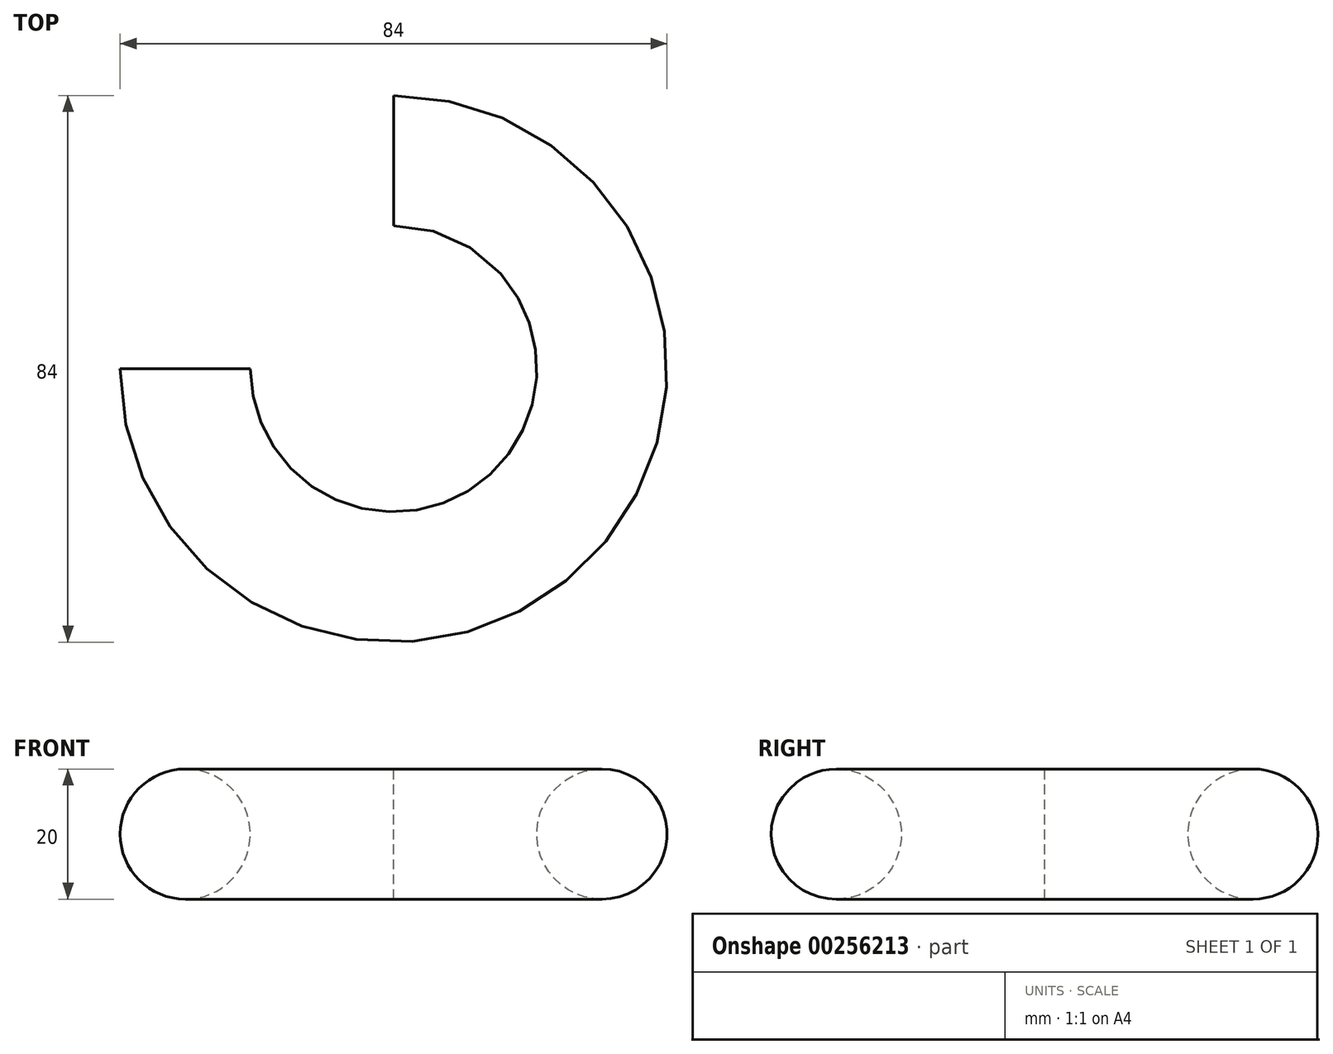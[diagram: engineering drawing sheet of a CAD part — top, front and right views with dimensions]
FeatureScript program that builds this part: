
annotation { "Feature Type Name" : "Feature", "Feature Type Description" : "" }
export const myFeature = defineFeature(function(context is Context, id is Id, definition is map)
    precondition{}
    {
        {
            var Q0;
            Q0=qCreatedBy(makeId("Right.planeOp"),FACE);
            var sketch = newSketch(context, id + "F0", { "sketchPlane" : qUnion([Q0])});
            skCircle(sketch, "E0", {"center": v(32, 0) * mm, "radius": 10 * mm});
            skLineSegment(sketch, "E1", {"start": v(0, 66.41) * mm, "end": v(0, -57.8) * mm});
            skLineSegment(sketch, "E2", {"start": v(0, -57.8) * mm, "end": v(0, 66.41) * mm, "construction": true});
            skSolve(sketch);
        }
        {
            var Q0;
            Q0=makeQuery(id+"F0.imprint","IMPRINT",FACE,{"disambiguationData":[TD([[makeQuery(id+"F0.imprint","IMPRINT",EDGE,{"derivedFrom":sQuery(id+"F0.wireOp",EDGE,"E0")}),1.0]])]});
            var Q1;
            Q1=sQuery(id+"F0.wireOp",EDGE,"E1");
            revolve(context, id + "F1", {"entities" : qUnion([Q0]), "axis" : qUnion([Q1]), "revolveType" : RevolveType.ONE_DIRECTION, "angle" : 270 * degree});
        }
    });
